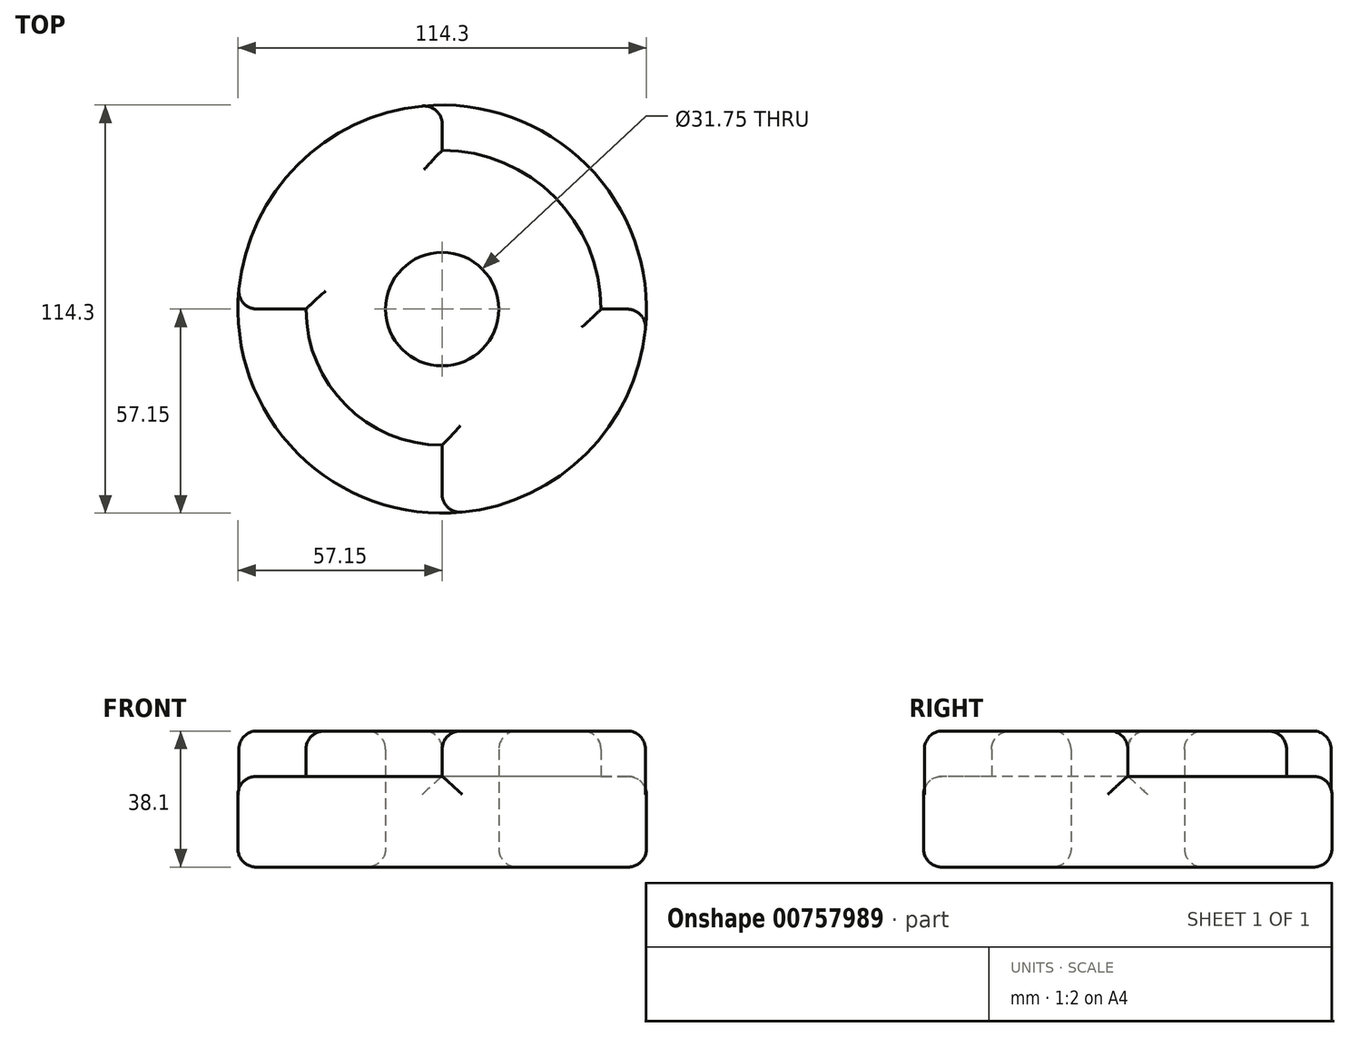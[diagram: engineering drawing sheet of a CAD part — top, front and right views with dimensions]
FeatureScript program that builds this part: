
annotation { "Feature Type Name" : "Feature", "Feature Type Description" : "" }
export const myFeature = defineFeature(function(context is Context, id is Id, definition is map)
    precondition{}
    {
        {
            var Q0;
            Q0=qCreatedBy(makeId("Top.planeOp"),FACE);
            var sketch = newSketch(context, id + "F0", { "sketchPlane" : qUnion([Q0])});
            skCircle(sketch, "E0", {"center": v(0, 0) * mm, "radius": 57.15 * mm});
            skSolve(sketch);
        }
        {
            var Q0;
            Q0=makeQuery(id+"F0.imprint","IMPRINT",FACE,{"disambiguationData":[TD([[makeQuery(id+"F0.imprint","IMPRINT",EDGE,{"derivedFrom":sQuery(id+"F0.wireOp",EDGE,"E0")}),1.0]])]});
            extrude(context, id + "F1", {"entities" : qUnion([Q0]), "depth" : 25.4 * mm, "offsetDistance" : 25.4 * mm});
        }
        {
            var Q0;
            Q0=makeQuery(id+"F1.opExtrude","CAP_FACE",FACE,{"disambiguationData":[OSD([sQuery(id+"F0.wireOp",EDGE,"E0")])],"isStart":false});
            var sketch = newSketch(context, id + "F2", { "sketchPlane" : qUnion([Q0])});
            skLineSegment(sketch, "E1", {"start": v(44.45, 0) * mm, "end": v(57.15, 0) * mm});
            skLineSegment(sketch, "E2", {"start": v(0, 44.45) * mm, "end": v(0, 57.15) * mm});
            skLineSegment(sketch, "E3", {"start": v(-38.1, 0) * mm, "end": v(-57.15, 0) * mm});
            skLineSegment(sketch, "E4", {"start": v(0, -38.1) * mm, "end": v(0, -57.15) * mm});
            skArc(sketch, "E5", {"start": v(-57.15, 0) * mm, "mid": v(-40.41, 40.41) * mm, "end": v(0, 57.15) * mm});
            skArc(sketch, "E6", {"start": v(0, 44.45) * mm, "mid": v(31.43, 31.43) * mm, "end": v(44.45, 0) * mm});
            skArc(sketch, "E7", {"start": v(57.15, 0) * mm, "mid": v(40.41, -40.41) * mm, "end": v(0, -57.15) * mm});
            skArc(sketch, "E8", {"start": v(0, -38.1) * mm, "mid": v(-26.94, -26.94) * mm, "end": v(-38.1, 0) * mm});
            skSolve(sketch);
        }
        {
            var Q0;
            Q0=makeQuery(id+"F2.imprint","IMPRINT",FACE,{"disambiguationData":[TD([[makeQuery(id+"F2.imprint","IMPRINT",EDGE,{"derivedFrom":sQuery(id+"F2.wireOp",EDGE,"E1")}),-1.0]])]});
            extrude(context, id + "F3", {"entities" : qUnion([Q0]), "operationType" : NewBodyOperationType.ADD, "depth" : 12.7 * mm, "offsetDistance" : 25.4 * mm});
        }
        {
            var Q0;
            Q0=sQuery(id+"F0.wireOp",VERTEX,"E0.center");
            var Q1;
            Q1=makeQuery(id+"F1.opExtrude","SWEPT_BODY",BODY,{"disambiguationData":[OSD([sQuery(id+"F0.wireOp",EDGE,"E0")])]});
            hole(context, id + "F4", {"style" : HoleStyle.SIMPLE, "endStyle" : HoleEndStyle.THROUGH, "oppositeDirection" : true, "holeDiameter" : 31.75 * mm, "majorDiameter" : 6.35 * mm, "isTappedThrough" : true, "tappedDepth" : 12.7 * mm, "tapClearance" : 3, "locations" : qUnion([Q0]), "scope" : qUnion([Q1])});
        }
        {
            var Q0;
            Q0=makeQuery(id+"F4.hole-0.boolean.opBoolean","COPY",FACE,{"derivedFrom":makeQuery(id+"F4.hole-0.opRevolve","SWEPT_FACE",FACE,{"disambiguationData":[OSD([sQuery(id+"F4.hole-0.sketch.wireOp",EDGE,"core_line_2")])]})});
            var Q1;
            Q1=makeQuery(id+"F3.opExtrude","CAP_FACE",FACE,{"disambiguationData":[OSD([sQuery(id+"F2.wireOp",EDGE,"E1"),sQuery(id+"F2.wireOp",EDGE,"E2"),sQuery(id+"F2.wireOp",EDGE,"E3"),sQuery(id+"F2.wireOp",EDGE,"E4"),sQuery(id+"F2.wireOp",EDGE,"E5"),sQuery(id+"F2.wireOp",EDGE,"E6"),sQuery(id+"F2.wireOp",EDGE,"E7"),sQuery(id+"F2.wireOp",EDGE,"E8")])],"isStart":false});
            fillet(context, id + "F5", {"entities" : qUnion([Q0, Q1]), "radius" : 5.08 * mm, "tangentPropagation" : true, "allowEdgeOverflow" : false});
        }
        {
            var Q0;
            Q0=makeQuery(id+"F3.boolean.opBoolean","MERGE",FACE,{"derivedFrom":[makeQuery(id+"F1.opExtrude","SWEPT_FACE",FACE,{"disambiguationData":[OSD([sQuery(id+"F0.wireOp",EDGE,"E0")])]}),makeQuery(id+"F3.opExtrude","SWEPT_FACE",FACE,{"disambiguationData":[OSD([sQuery(id+"F2.wireOp",EDGE,"E5")])]}),makeQuery(id+"F3.opExtrude","SWEPT_FACE",FACE,{"disambiguationData":[OSD([sQuery(id+"F2.wireOp",EDGE,"E7")])]})]});
            var Q1;
            Q1=makeQuery(id+"F1.opExtrude","CAP_FACE",FACE,{"disambiguationData":[OSD([sQuery(id+"F0.wireOp",EDGE,"E0")])],"isStart":true});
            fillet(context, id + "F6", {"entities" : qUnion([Q0, Q1]), "radius" : 5.08 * mm, "tangentPropagation" : true, "allowEdgeOverflow" : false});
        }
    });
